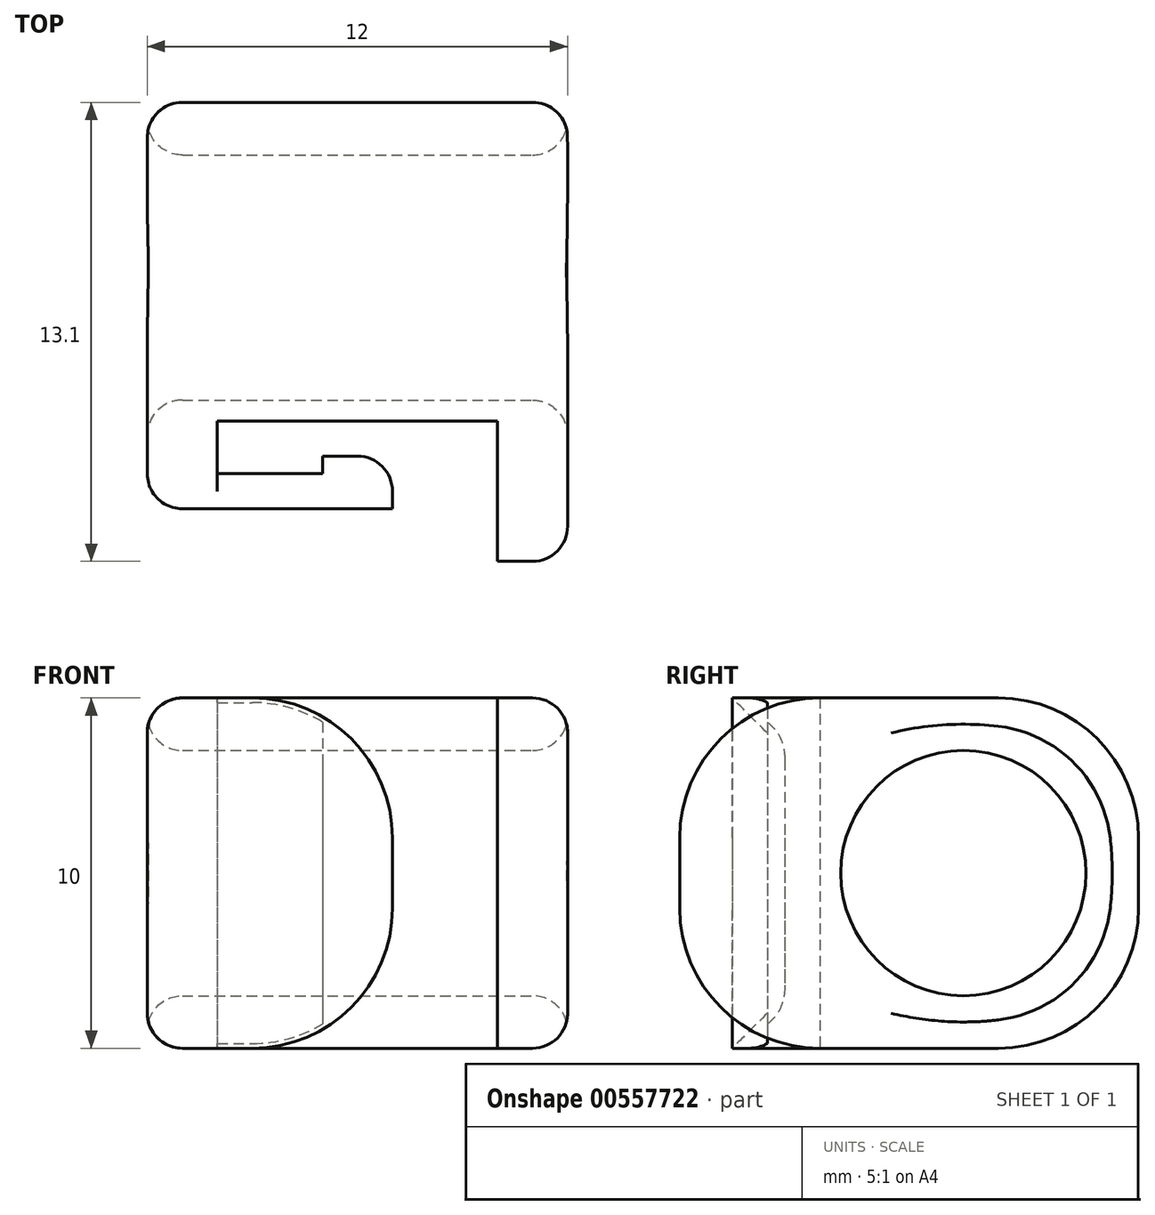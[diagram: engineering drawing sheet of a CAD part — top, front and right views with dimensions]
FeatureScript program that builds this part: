
annotation { "Feature Type Name" : "Feature", "Feature Type Description" : "" }
export const myFeature = defineFeature(function(context is Context, id is Id, definition is map)
    precondition{}
    {
        {
            var Q0;
            Q0=qCreatedBy(makeId("Top.planeOp"),FACE);
            var sketch = newSketch(context, id + "F0", { "sketchPlane" : qUnion([Q0])});
            skLineSegment(sketch, "E0", {"start": v(2, -1) * mm, "end": v(2, -2.5) * mm});
            skLineSegment(sketch, "E1", {"start": v(7, -2) * mm, "end": v(7, -3.5) * mm});
            skLineSegment(sketch, "E2", {"start": v(7, -3.5) * mm, "end": v(0, -3.5) * mm});
            skLineSegment(sketch, "E3", {"start": v(0, -3.5) * mm, "end": v(0, 0) * mm});
            skLineSegment(sketch, "E4", {"start": v(0, 0) * mm, "end": v(0, 0) * mm});
            skLineSegment(sketch, "E5", {"start": v(0, 0) * mm, "end": v(0, 8.1) * mm});
            skLineSegment(sketch, "E6", {"start": v(0, 8.1) * mm, "end": v(12, 8.1) * mm});
            skLineSegment(sketch, "E7", {"start": v(12, 8.1) * mm, "end": v(12, 0) * mm});
            skLineSegment(sketch, "E8", {"start": v(5, -1) * mm, "end": v(2, -1) * mm});
            skLineSegment(sketch, "E9", {"start": v(2, -2.5) * mm, "end": v(5, -2.5) * mm});
            skLineSegment(sketch, "E10", {"start": v(5, -2.5) * mm, "end": v(5, -2) * mm});
            skLineSegment(sketch, "E11", {"start": v(5, -2) * mm, "end": v(7, -2) * mm});
            skLineSegment(sketch, "E12", {"start": v(12, 0) * mm, "end": v(12, 0) * mm});
            skLineSegment(sketch, "E13", {"start": v(12, 0) * mm, "end": v(12, -5) * mm});
            skLineSegment(sketch, "E14", {"start": v(12, -5) * mm, "end": v(10, -5) * mm});
            skLineSegment(sketch, "E15", {"start": v(10, -5) * mm, "end": v(10, -1) * mm});
            skLineSegment(sketch, "E16", {"start": v(10, -1) * mm, "end": v(5, -1) * mm});
            skSolve(sketch);
        }
        {
            var Q0;
            Q0=makeQuery(id+"F0.imprint","IMPRINT",FACE,{"disambiguationData":[TD([[makeQuery(id+"F0.imprint","IMPRINT",EDGE,{"derivedFrom":sQuery(id+"F0.wireOp",EDGE,"E0")}),-1.0]])]});
            extrude(context, id + "F1", {"entities" : qUnion([Q0]), "endBound" : BoundingType.SYMMETRIC, "depth" : 10 * mm, "offsetDistance" : 25 * mm});
        }
        {
            var Q0;
            Q0=makeQuery(id+"F1.opExtrude","SWEPT_FACE",FACE,{"disambiguationData":[OSD([sQuery(id+"F0.wireOp",EDGE,"E7"),sQuery(id+"F0.wireOp",EDGE,"1kXGVvJr-JPgg-7YMV-aefA-PGxPgHNlz1uc")])]});
            var sketch = newSketch(context, id + "F2", { "sketchPlane" : qUnion([Q0])});
            skCircle(sketch, "E17", {"center": v(3.1, 0) * mm, "radius": 3.5 * mm});
            skLineSegment(sketch, "E18", {"start": v(8.1, 0) * mm, "end": v(3.1, 0) * mm, "construction": true});
            skSolve(sketch);
        }
        {
            var Q0;
            Q0=makeQuery(id+"F2.imprint","IMPRINT",FACE,{"disambiguationData":[TD([[makeQuery(id+"F2.imprint","IMPRINT",EDGE,{"derivedFrom":sQuery(id+"F2.wireOp",EDGE,"E17")}),1.0]])]});
            extrude(context, id + "F3", {"entities" : qUnion([Q0]), "operationType" : NewBodyOperationType.REMOVE, "endBound" : BoundingType.SYMMETRIC, "oppositeDirection" : true, "depth" : 25 * mm, "offsetDistance" : 25 * mm});
        }
        {
            var Q0;
            Q0=makeQuery(id+"F1.opExtrude","CAP_EDGE",EDGE,{"disambiguationData":[OSD([sQuery(id+"F0.wireOp",EDGE,"E6")])],"isStart":true});
            var Q1;
            Q1=makeQuery(id+"F1.opExtrude","CAP_EDGE",EDGE,{"disambiguationData":[OSD([sQuery(id+"F0.wireOp",EDGE,"E6")])],"isStart":false});
            var Q2;
            Q2=makeQuery(id+"F1.opExtrude","CAP_EDGE",EDGE,{"disambiguationData":[OSD([sQuery(id+"F0.wireOp",EDGE,"E14")])],"isStart":true});
            var Q3;
            Q3=makeQuery(id+"F1.opExtrude","CAP_EDGE",EDGE,{"disambiguationData":[OSD([sQuery(id+"F0.wireOp",EDGE,"E14")])],"isStart":false});
            var Q4;
            Q4=makeQuery(id+"F1.opExtrude","CAP_EDGE",EDGE,{"disambiguationData":[OSD([sQuery(id+"F0.wireOp",EDGE,"E1")])],"isStart":false});
            var Q5;
            Q5=makeQuery(id+"F1.opExtrude","CAP_EDGE",EDGE,{"disambiguationData":[OSD([sQuery(id+"F0.wireOp",EDGE,"E1")])],"isStart":true});
            fillet(context, id + "F4", {"entities" : qUnion([Q0, Q1, Q2, Q3, Q4, Q5]), "radius" : 4 * mm, "tangentPropagation" : true, "allowEdgeOverflow" : false});
        }
        {
            var Q0;
            Q0=makeQuery(id+"F1.opExtrude","CAP_EDGE",EDGE,{"disambiguationData":[OSD([sQuery(id+"F0.wireOp",EDGE,"E3")])],"isStart":false});
            var Q1;
            Q1=makeQuery(id+"F1.opExtrude","CAP_EDGE",EDGE,{"disambiguationData":[OSD([sQuery(id+"F0.wireOp",EDGE,"E3")])],"isStart":true});
            var Q2;
            Q2=makeQuery(id+"F1.opExtrude","SWEPT_FACE",FACE,{"disambiguationData":[OSD([sQuery(id+"F0.wireOp",EDGE,"E3")])]});
            var Q3;
            Q3=makeQuery(id+"F1.opExtrude","SWEPT_FACE",FACE,{"disambiguationData":[OSD([sQuery(id+"F0.wireOp",EDGE,"E13")])]});
            var Q4;
            Q4=makeQuery(id+"F1.opExtrude","SWEPT_EDGE",EDGE,{"disambiguationData":[OSD([sQuery(id+"F0.wireOp",EDGE,"E1"),sQuery(id+"F0.wireOp",EDGE,"E11")])]});
            fillet(context, id + "F5", {"entities" : qUnion([Q0, Q1, Q2, Q3, Q4]), "radius" : 1 * mm, "tangentPropagation" : true, "allowEdgeOverflow" : false});
        }
    });
